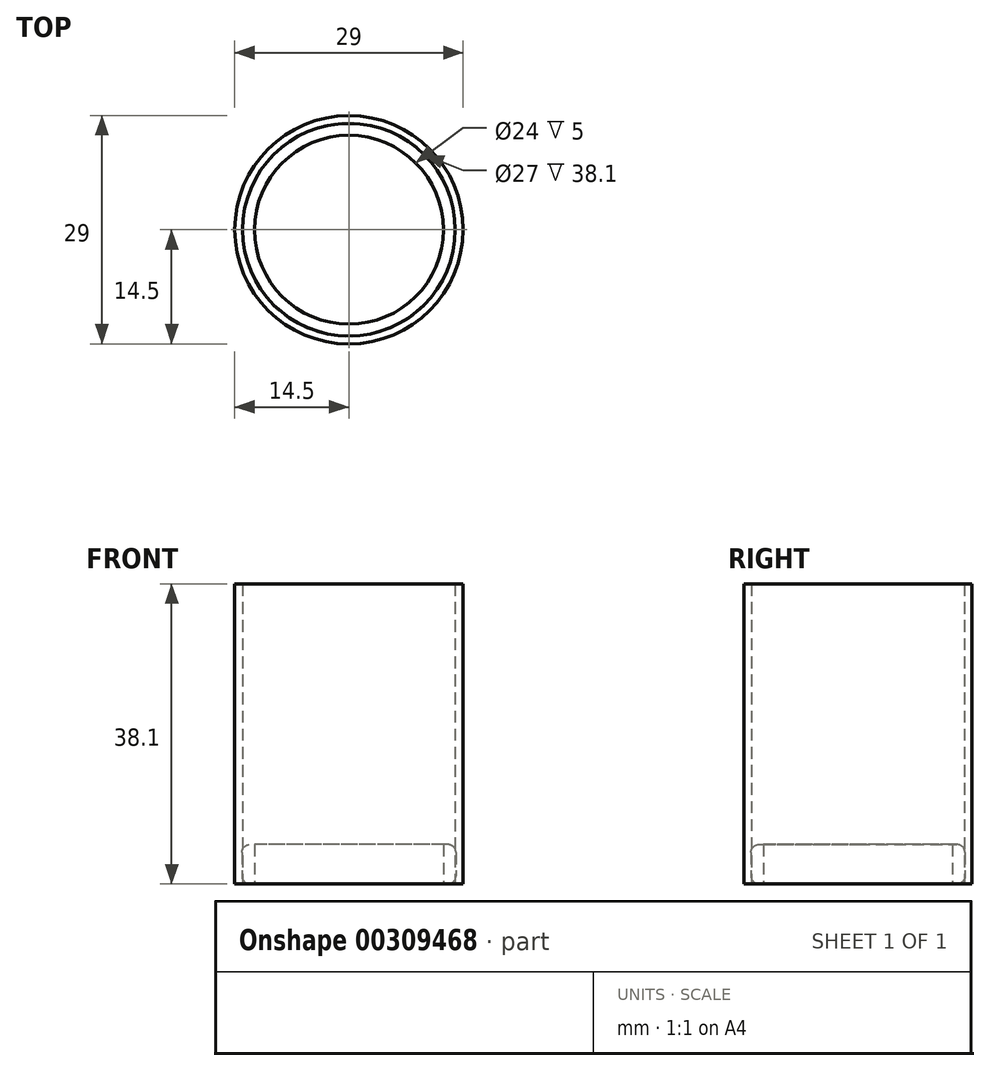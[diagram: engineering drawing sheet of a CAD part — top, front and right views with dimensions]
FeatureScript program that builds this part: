
annotation { "Feature Type Name" : "Feature", "Feature Type Description" : "" }
export const myFeature = defineFeature(function(context is Context, id is Id, definition is map)
    precondition{}
    {
        {
            var Q0;
            Q0=qCreatedBy(makeId("Top.planeOp"),FACE);
            var sketch = newSketch(context, id + "F0", { "sketchPlane" : qUnion([Q0])});
            skCircle(sketch, "E0", {"center": v(0, 0) * mm, "radius": 62.03 * mm});
            skCircle(sketch, "E1", {"center": v(0, 0) * mm, "radius": 57.77 * mm});
            skLineSegment(sketch, "E2", {"start": v(0, -57.77) * mm, "end": v(0, -62.03) * mm});
            skSolve(sketch);
        }
        {
            var Q0;
            Q0=qCreatedBy(makeId("Top.planeOp"),FACE);
            cPlane(context, id + "F1", {"entities" : qUnion([Q0]), "cplaneType" : CPlaneType.OFFSET, "offset" : 76.2 * mm, "width" : 152.4 * mm, "height" : 152.4 * mm});
        }
        {
            var Q0;
            Q0=qCreatedBy(id+"F1.planeOp",FACE);
            var sketch = newSketch(context, id + "F2", { "sketchPlane" : qUnion([Q0])});
            skCircle(sketch, "E3", {"center": v(0, 0) * mm, "radius": 13.5 * mm});
            skCircle(sketch, "E4", {"center": v(0, 0) * mm, "radius": 14.5 * mm});
            skSolve(sketch);
        }
        {
            var Q0;
            Q0=qCreatedBy(makeId("Front.planeOp"),FACE);
            var sketch = newSketch(context, id + "F3", { "sketchPlane" : qUnion([Q0])});
            skLineSegment(sketch, "E5", {"start": v(12.74, 77.12) * mm, "end": v(56.93, 0) * mm});
            skSolve(sketch);
        }
        {
            var Q0;
            Q0=sQuery(id+"F3.wireOp",EDGE,"E5");
            var Q1;
            Q1=sQuery(id+"F2.wireOp",EDGE,"E3");
            revolve(context, id + "F4", {"bodyType" : ToolBodyType.SURFACE, "surfaceEntities" : qUnion([Q0]), "axis" : qUnion([Q1]), "revolveType" : RevolveType.FULL});
        }
        {
            var Q0;
            Q0=qCreatedBy(makeId("Front.planeOp"),FACE);
            var sketch = newSketch(context, id + "F5", { "sketchPlane" : qUnion([Q0])});
            skLineSegment(sketch, "E6", {"start": v(-62.28, 0) * mm, "end": v(-15.75, 75.4) * mm});
            skSolve(sketch);
        }
        {
            var Q0;
            Q0=sQuery(id+"F5.wireOp",EDGE,"E6");
            var Q1;
            Q1=sQuery(id+"F2.wireOp",EDGE,"E4");
            revolve(context, id + "F6", {"bodyType" : ToolBodyType.SURFACE, "surfaceEntities" : qUnion([Q0]), "axis" : qUnion([Q1]), "revolveType" : RevolveType.FULL});
        }
        {
            var Q0;
            Q0=sQuery(id+"F0.wireOp",EDGE,"E2");
            var Q1;
            Q1=sQuery(id+"F0.wireOp",EDGE,"E1");
            revolve(context, id + "F7", {"bodyType" : ToolBodyType.SURFACE, "surfaceEntities" : qUnion([Q0]), "axis" : qUnion([Q1]), "revolveType" : RevolveType.FULL});
        }
        {
            var Q0;
            Q0=makeQuery(id+"F2.imprint","IMPRINT",FACE,{"disambiguationData":[TD([[makeQuery(id+"F2.imprint","IMPRINT",EDGE,{"derivedFrom":sQuery(id+"F2.wireOp",EDGE,"E3")}),-1.0]])]});
            extrude(context, id + "F8", {"entities" : qUnion([Q0]), "depth" : 38.1 * mm});
        }
        {
            var Q0;
            Q0=makeQuery(id+"F8.opExtrude","CAP_FACE",FACE,{"disambiguationData":[OSD([sQuery(id+"F2.wireOp",EDGE,"E3"),sQuery(id+"F2.wireOp",EDGE,"E4")])],"isStart":false});
            var sketch = newSketch(context, id + "F9", { "sketchPlane" : qUnion([Q0])});
            skCircle(sketch, "E7", {"center": v(0, 0) * mm, "radius": 13 * mm});
            skSolve(sketch);
        }
        {
            var Q0;
            Q0=qCreatedBy(id+"F1.planeOp",FACE);
            var sketch = newSketch(context, id + "F10", { "sketchPlane" : qUnion([Q0])});
            skCircle(sketch, "E8", {"center": v(0, 0) * mm, "radius": 13.6 * mm});
            skCircle(sketch, "E9", {"center": v(0, 0) * mm, "radius": 12 * mm});
            skSolve(sketch);
        }
        {
            var Q0;
            Q0=qSketchRegion(id+"F10",true);
            extrude(context, id + "F11", {"entities" : qUnion([Q0]), "depth" : 5 * mm});
        }
        {
            var Q0;
            Q0=makeQuery(id+"F11.opExtrude","CAP_EDGE",EDGE,{"disambiguationData":[OSD([sQuery(id+"F10.wireOp",EDGE,"E8")])],"isStart":true});
            var Q1;
            Q1=makeQuery(id+"F11.opExtrude","CAP_EDGE",EDGE,{"disambiguationData":[OSD([sQuery(id+"F10.wireOp",EDGE,"E8")])],"isStart":false});
            fillet(context, id + "F12", {"entities" : qUnion([Q0, Q1]), "radius" : 1 * mm, "tangentPropagation" : true, "allowEdgeOverflow" : false});
        }
    });
